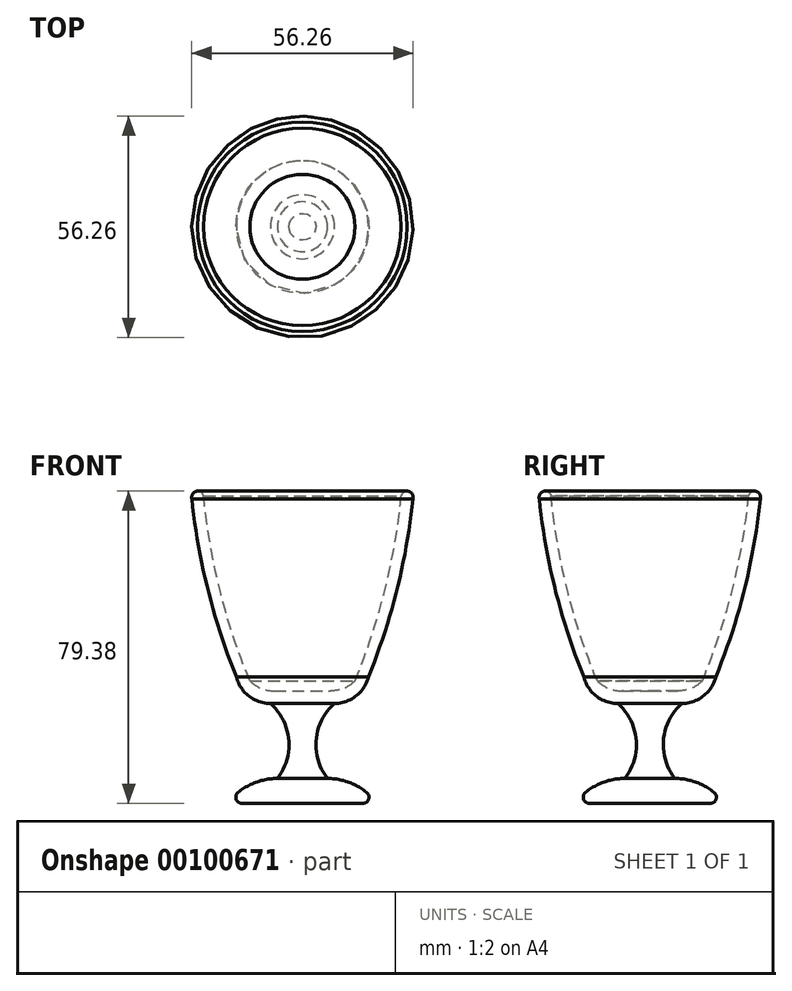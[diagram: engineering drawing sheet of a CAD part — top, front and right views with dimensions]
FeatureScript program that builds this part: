
annotation { "Feature Type Name" : "Feature", "Feature Type Description" : "" }
export const myFeature = defineFeature(function(context is Context, id is Id, definition is map)
    precondition{}
    {
        {
            var Q0;
            Q0=qCreatedBy(makeId("Front.planeOp"),FACE);
            var sketch = newSketch(context, id + "F0", { "sketchPlane" : qUnion([Q0])});
            skLineSegment(sketch, "E0", {"start": v(-26.61, 44.25) * mm, "end": v(-26.7, 44.25) * mm});
            skArc(sketch, "E1", {"start": v(-6.42, -28.78) * mm, "mid": v(-11.71, -29.69) * mm, "end": v(-16.4, -32.3) * mm});
            skLineSegment(sketch, "E2", {"start": v(-15.4, -35.13) * mm, "end": v(-0.07, -35.13) * mm});
            skPoint(sketch, "E3.visualSharp", {"position": v(-12.77, -6.55) * mm});
            skArc(sketch, "E3.filletArc", {"start": v(-13.4, -4.04) * mm, "mid": v(-10.54, -5.9) * mm, "end": v(-7.2, -6.55) * mm});
            skPoint(sketch, "E4.visualSharp", {"position": v(-15.15, -9.73) * mm});
            skArc(sketch, "E4.filletArc", {"start": v(-16.83, -3) * mm, "mid": v(-13.68, -7.85) * mm, "end": v(-8.2, -9.73) * mm});
            skPoint(sketch, "E5.visualSharp", {"position": v(-25.47, 44.25) * mm});
            skArc(sketch, "E5.filletArc", {"start": v(-25.17, 43.04) * mm, "mid": v(-25.73, 43.9) * mm, "end": v(-26.7, 44.25) * mm});
            skPoint(sketch, "E6.visualSharp", {"position": v(-28.64, 44.25) * mm});
            skArc(sketch, "E6.filletArc", {"start": v(-26.61, 44.25) * mm, "mid": v(-27.86, 43.64) * mm, "end": v(-28.15, 42.27) * mm});
            skPoint(sketch, "E7.visualSharp", {"position": v(-19.12, -35.13) * mm});
            skArc(sketch, "E7.filletArc", {"start": v(-16.4, -32.3) * mm, "mid": v(-16.9, -34.07) * mm, "end": v(-15.4, -35.13) * mm});
            skLineSegment(sketch, "E8", {"start": v(-0.07, -6.55) * mm, "end": v(-0.07, -35.13) * mm});
            skLineSegment(sketch, "E9", {"start": v(-0.07, -6.55) * mm, "end": v(-0.07, 24.1) * mm, "construction": true});
            skArc(sketch, "E10", {"start": v(-25.17, 43.04) * mm, "mid": v(-21.02, 19.07) * mm, "end": v(-13.4, -4.04) * mm});
            skArc(sketch, "E11", {"start": v(-28.15, 42.27) * mm, "mid": v(-24.1, 19.24) * mm, "end": v(-16.83, -3) * mm});
            skArc(sketch, "E12", {"start": v(-6.42, -28.78) * mm, "mid": v(-3.55, -18.9) * mm, "end": v(-8.2, -9.73) * mm});
            skLineSegment(sketch, "E13", {"start": v(-7.2, -6.55) * mm, "end": v(-0.07, -6.55) * mm});
            skSolve(sketch);
        }
        {
            var Q0;
            Q0=makeQuery(id+"F0.imprint","IMPRINT",FACE,{"disambiguationData":[TD([[makeQuery(id+"F0.imprint","IMPRINT",EDGE,{"derivedFrom":sQuery(id+"F0.wireOp",EDGE,"E1")}),1.0]])]});
            var Q1;
            Q1=sQuery(id+"F0.wireOp",EDGE,"E9");
            revolve(context, id + "F1", {"entities" : qUnion([Q0]), "axis" : qUnion([Q1]), "revolveType" : RevolveType.FULL});
        }
    });
